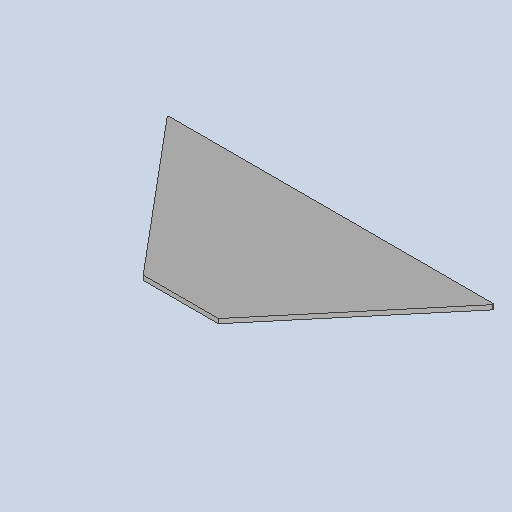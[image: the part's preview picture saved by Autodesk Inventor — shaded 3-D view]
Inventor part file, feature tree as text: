
AUTODESK INVENTOR PART (.ipt)
format: ipt  version: 2025 (Build 290162010, 162A)  size: 268,288 bytes
history: native  units: mm
features: other x2, sheet_metal_op x1, chamfer x1, sketch x1
ambient origin geometry x8: Origin, YZ Plane, XZ Plane, XY Plane, X Axis, Y Axis, Z Axis, Center Point
bodies: Solid1 (feature_tree)
feature tree (5):
  sheet_metal_op  "Face1"
  chamfer  "Chamfer1"  Distance=50.0mm
  sketch  "Sketch1"  dims[d0=100.0mm d1=50.0mm d2=217.819926mm d3=3.0mm d4=22.68928mm d5=1.0mm d6=2.0mm d7=45.0deg]
  other  "Plate1"
  other  "Definition1"
